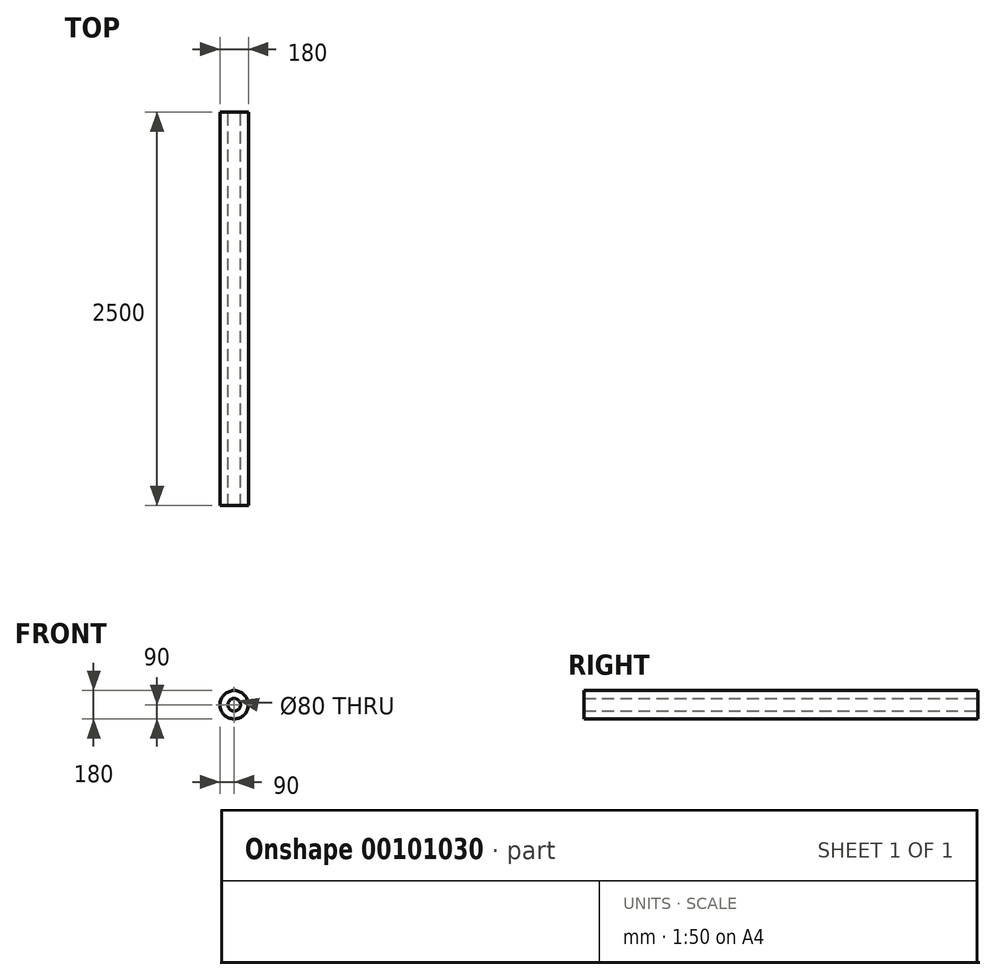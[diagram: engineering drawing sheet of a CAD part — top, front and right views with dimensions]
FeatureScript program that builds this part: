
annotation { "Feature Type Name" : "Feature", "Feature Type Description" : "" }
export const myFeature = defineFeature(function(context is Context, id is Id, definition is map)
    precondition{}
    {
        {
            var Q0;
            Q0=qCreatedBy(makeId("Front.planeOp"),FACE);
            var sketch = newSketch(context, id + "F0", { "sketchPlane" : qUnion([Q0])});
            skCircle(sketch, "E0", {"center": v(0, 0) * mm, "radius": 40 * mm});
            skCircle(sketch, "E1", {"center": v(0, 0) * mm, "radius": 90 * mm});
            skSolve(sketch);
        }
        {
            var Q0;
            Q0=makeQuery(id+"F0.imprint","IMPRINT",FACE,{"disambiguationData":[TD([[makeQuery(id+"F0.imprint","IMPRINT",EDGE,{"derivedFrom":sQuery(id+"F0.wireOp",EDGE,"E0")}),-1.0]])]});
            extrude(context, id + "F1", {"entities" : qUnion([Q0]), "depth" : 2500 * mm});
        }
    });
